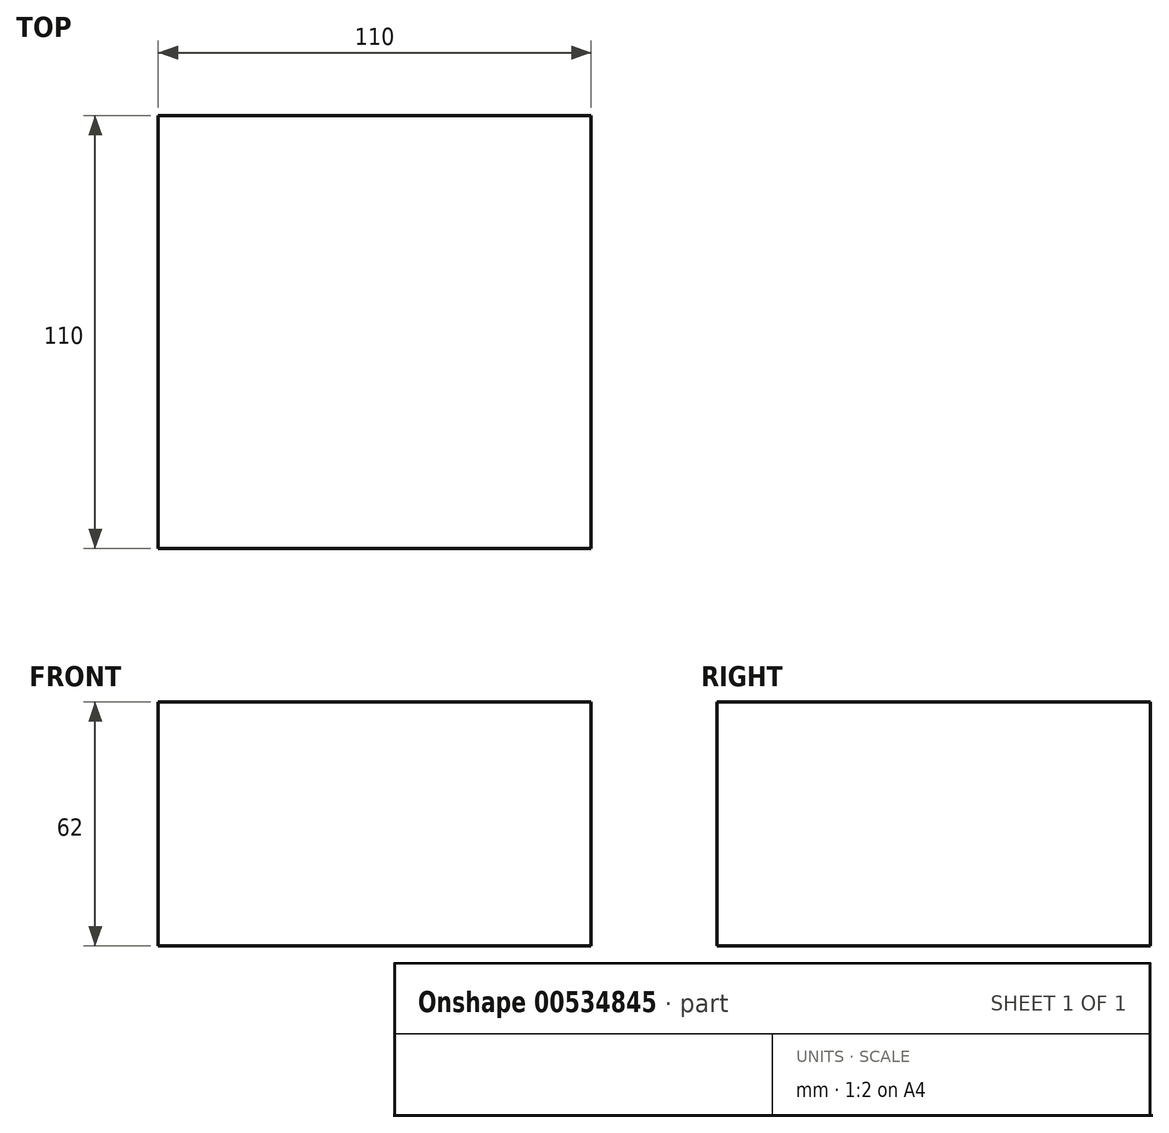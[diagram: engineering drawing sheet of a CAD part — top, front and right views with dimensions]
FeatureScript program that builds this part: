
annotation { "Feature Type Name" : "Feature", "Feature Type Description" : "" }
export const myFeature = defineFeature(function(context is Context, id is Id, definition is map)
    precondition{}
    {
        {
            var Q0;
            Q0=qCreatedBy(makeId("Top.planeOp"),FACE);
            var sketch = newSketch(context, id + "F0", { "sketchPlane" : qUnion([Q0])});
            skLineSegment(sketch, "E0.bottom", {"start": v(55, -55) * mm, "end": v(-55, -55) * mm});
            skLineSegment(sketch, "E0.top", {"start": v(55, 55) * mm, "end": v(-55, 55) * mm});
            skLineSegment(sketch, "E0.left", {"start": v(55, -55) * mm, "end": v(55, 55) * mm});
            skLineSegment(sketch, "E0.right", {"start": v(-55, -55) * mm, "end": v(-55, 55) * mm});
            skPoint(sketch, "E0.middle", {"position": v(0, 0) * mm});
            skSolve(sketch);
        }
        {
            var Q0;
            Q0=makeQuery(id+"F0.imprint","IMPRINT",FACE,{"disambiguationData":[TD([[makeQuery(id+"F0.imprint","IMPRINT",EDGE,{"derivedFrom":sQuery(id+"F0.wireOp",EDGE,"E0.bottom")}),-1.0]])]});
            extrude(context, id + "F1", {"entities" : qUnion([Q0]), "depth" : 62 * mm, "offsetDistance" : 25 * mm});
        }
    });
